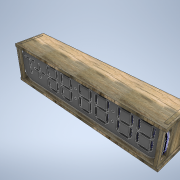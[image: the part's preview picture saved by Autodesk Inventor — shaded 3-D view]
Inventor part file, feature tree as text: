
AUTODESK INVENTOR PART (.ipt)
format: ipt  version: 2021 (Build 250183000, 183)  size: 3,486,208 bytes
history: native  units: in
note: dims shown in document units (in); Inventor stores cm internally (conversion verified against a paired STEP export)
features: other x71, extrude x17, sketch x16, imported_body x1
ambient origin geometry x8: Origin, YZ Plane, XZ Plane, XY Plane, X Axis, Y Axis, Z Axis, Center Point
bodies: Body1 (feature_tree), Body2 (feature_tree), Body3 (feature_tree), Body4 (feature_tree), Body5 (feature_tree), Body6 (feature_tree), Body7 (feature_tree)
feature tree (105):
  other  "Clock Face"
  other  "Blocks"
  extrude  "Extrusion1"  TaperAngle=135.0deg  [1 undecoded]
  extrude  "Extrusion3"  TaperAngle=135.0deg  [1 undecoded]
  extrude  "Extrusion5"  Depth=0.0433in
  extrude  "Extrusion6"  Depth=0.0433in
  extrude  "Extrusion9"  Depth=0.0433in
  extrude  "Extrusion7"  Depth=0.0433in
  extrude  "Extrusion10"  Depth=0.0433in
  extrude  "Extrusion8"  Depth=0.0433in
  extrude  "Extrusion13"  Depth=0.126in
  extrude  "Extrusion14"  Depth=0.126in
  extrude  "Extrusion15"  Depth=2.2441in
  extrude  "Extrusion16"  Depth=0.126in
  extrude  "Extrusion17"  Depth=0.126in
  extrude  "Extrusion18"  Depth=0.1969in
  extrude  "Extrusion19"  Depth=0.8661in
  extrude  "Extrusion20"  Depth=0.0866in
  extrude  "Extrusion21"  Depth=0.0118in
  other  "Single Segment"
  other  "7 Segment Digit"
  other  "Slanted Segment Large"
  other  "+ sign"
  other  "Dot"
  other  "Clock Face with T +-"
  other  "Clock Front Face Outline"
  other  "Small Segmemt"
  sketch  "Sketch5"  dims[d10=62.9921in d11=78.7402in d29=0.1969in d30=0.0in]
  sketch  "Sketch8"  dims[d105=0.0866in d108=0.0866in d111=0.0866in d112=0.0866in d113=0.0866in d114=0.0866in d115=0.0866in d116=0.0394in d117=0.1969in d121=0.0866in d122=0.0866in d126=135.0deg]
  other  "ClockBackface"
  sketch  "Sketch9"  dims[d127=0.8661in d128=135.0deg]
  sketch  "Sketch10"  dims[d129=0.0984in]
  other  "Backplace"
  sketch  "Sketch11"  dims[d131=0.0433in d132=0.0433in d137=0.0433in d138=0.0433in d139=0.0433in d140=0.0433in]
  other  "FrontCover"
  other  "7SegmentOutline"
  sketch  "Sketch15"  dims[d141=0.0433in d142=0.0433in]
  other  "Cable Trench"
  other  "Cable Trench Long"
  other  "CableCutouts"
  sketch  "Sketch17"  dims[d143=0.0433in d144=0.0433in]
  sketch  "Sketch20"  dims[d145=0.0433in d146=0.0433in]
  imported_body  "Base"
  sketch  "Sketch21"  dims[d150=0.0433in d151=0.0433in]
  other  "Side Panels"
  sketch  "Sketch22"  dims[d152=0.0433in d153=0.0433in]
  sketch  "Sketch23"  dims[d294=0.126in d295=0.126in]
  sketch  "Sketch25"  dims[d296=0.315in d297=0.126in]
  sketch  "Sketch26"  dims[d298=0.126in d299=2.2441in]
  other  "Top Panel"
  sketch  "Sketch27"  dims[d304=0.126in d305=0.126in]
  sketch  "Sketch28"  dims[d306=0.126in d307=0.126in]
  sketch  "Sketch29"  dims[d311=0.0787in d312=0.0787in d314=0.0787in d315=0.0787in d316=0.0787in d317=0.0787in d318=0.0787in d319=0.0787in d320=0.0394in d321=0.0394in d322=0.0394in d323=0.0394in d348=0.1969in d349=0.8661in d350=0.0866in d352=0.0118in d353=0.0118in d358=0.0118in d359=0.0118in d360=0.1969in d361=0.1969in d362=0.2953in d363=0.6693in d364=0.2953in d366=0.2953in d367=0.0in d368=0.0in d369=0.0in d370=0.0in d371=0.0in d372=0.5906in d373=0.0in d374=0.6299in d375=0.2362in d376=0.2362in d377=0.5354in d378=0.6299in d379=0.2362in d380=0.5906in d381=0.0in d402=1.9528in d429=12.9921in d430=2.7559in d431=0.9843in d462=0.0866in d463=0.0866in d464=0.0866in d465=0.0866in d466=0.0866in d467=0.0866in d468=0.0866in d469=0.0394in d470=0.1969in d471=0.0866in d472=0.0866in d473=135.0deg d474=0.6299in d475=135.0deg d476=0.0984in d477=0.1969in d478=0.6299in d479=0.0866in d480=0.0118in d481=0.0118in d482=0.0118in d483=0.0118in d496=0.0787in d497=0.0787in d501=0.0394in d502=0.0394in d503=0.0in d504=0.0in d505=0.039in d506=0.039in d507=0.039in d508=0.039in d509=0.8661in d510=0.9843in d511=0.9685in d514=0.0394in d515=0.0394in d516=0.0394in d517=0.0394in d518=0.0in d519=0.039in d520=0.4331in d522=0.9449in d523=0.0in d524=0.0591in d525=0.315in d526=0.2913in d527=0.8661in d528=0.6575in d529=0.315in d530=0.1969in d531=0.0in d536=1.378in d537=6.4961in d538=6.4961in d539=1.378in d542=1.378in d543=6.4961in d544=0.1181in d545=0.0in d549=0.1181in d550=0.0in d551=1.378in d552=6.4961in d553=0.1181in d554=0.0in d555=1.378in d556=6.4961in d557=0.1181in d558=0.0in d564=0.2362in d1135=1.1732in d1136=1.1732in d1137=2.1496in d1138=0.0612in d1139=0.0612in d1140=0.0612in d1143=0.0612in d1144=0.0612in d1145=90.0deg d1146=0.0866in d1147=0.0236in d1150=0.0236in d1153=0.0236in d1154=0.0866in d1155=1.0197in d1156=1.0197in d1157=0.0866in d1158=0.0236in d1159=0.0866in d1160=0.0866in d1161=0.0236in d1162=0.0866in d1163=0.0866in d1164=0.0236in d1165=0.0866in d1166=0.0866in d1167=0.0236in d1168=0.0866in d1169=0.0866in d1170=0.0866in d1171=0.0866in d1172=0.0866in d1173=0.0866in d1175=0.1102in d1176=0.8661in d1177=0.8661in d1178=1.0197in d1179=0.0866in d1180=0.0236in d1181=0.0866in d1182=0.0866in d1183=0.0236in d1184=0.0866in d1188=0.0866in d1189=0.0236in d1190=0.0866in d1193=0.0866in d1194=0.0236in d1195=0.0in d1196=0.0in d1198=135.0deg d1199=0.0612in d1200=0.0866in d1201=0.0in d1202=0.0in d1205=0.0in d1206=0.0in d1207=0.0in d1208=135.0deg d1209=90.0deg d1210=90.0deg d1211=0.0866in d1212=0.0236in d1213=0.6603in d1214=0.6603in d1215=0.6603in d1216=90.0deg d1217=135.0deg d1218=0.6603in d1219=0.0394in d1221=135.0deg d1222=0.0394in d1223=0.0866in d1224=0.0866in d1225=0.0866in d1227=0.0866in d1228=0.0866in d1229=0.0866in d1230=0.0236in d1231=135.0deg d1232=90.0deg d1233=90.0deg d1234=135.0deg d1235=90.0deg d1236=90.0deg d1239=0.1102in d1240=0.2402in d1241=0.2402in d1242=0.2835in d1243=0.2835in d1244=0.2402in d1245=0.2402in d1246=0.0669in d1247=0.0669in d1248=0.0669in d1249=0.0669in d1250=0.0433in d1251=0.0433in d1252=0.8661in d1253=0.1535in d1254=90.0deg d1255=135.0deg d1256=45.0deg d1257=0.6603in d1258=0.0236in d1259=135.0deg d1260=135.0deg d1261=90.0deg d1262=0.0612in d1263=0.0866in d1264=0.0in d1265=0.0in d1266=0.0in d1267=0.0in d1268=0.0in d1269=0.0in d1270=0.0in d1271=0.0in d1272=0.0in d1273=0.0in d1274=0.0in d1275=0.0in d1276=0.0in d1277=0.0in d1278=0.0in d1279=0.0in d1280=0.0in d1281=0.0in d1282=0.0in d1283=0.0in d1292=0.0866in d1307=0.0394in d1308=0.0394in d1309=0.0394in d1310=0.0394in d1311=0.0394in d1312=0.0394in d1313=0.0394in d1314=0.2756in d1315=0.0197in d1316=0.0197in d1317=0.3445in d1318=0.0394in d1319=0.0394in d1320=0.0787in d1321=0.0866in d1322=0.0787in d1323=0.0787in d1344=0.0394in d1350=0.0866in d1351=0.0866in d1386=0.1181in d1387=0.0in d1390=0.0394in d1392=0.0118in d1393=0.0394in d1394=0.0394in d1395=0.0394in d1396=0.0394in d1397=0.1378in d1398=0.1349in d1399=0.0394in d1402=0.0787in d1425=0.0in d1429=0.0in d1431=0.0394in d1432=0.0394in d1507=0.0in d1508=0.0394in d1509=0.0394in d1510=0.0394in d1511=0.0394in d1513=0.0394in d1514=0.0394in d1515=0.0in d1516=0.0in d1517=0.0in d1518=0.0in d1519=0.0197in d1520=0.0197in d1521=0.1969in d1522=0.0394in d1523=0.0394in d1524=0.0394in d1525=0.1181in d1526=0.1181in d1527=0.0394in d1529=0.2741in d1530=0.0787in d1531=0.0787in d1532=0.0325in d1533=0.033in d1534=0.0787in d1535=0.0787in d1536=0.0325in d1537=0.0787in d1538=0.0787in d1539=0.0325in d1635=0.0787in d1636=0.0689in d1638=0.2756in d1641=0.315in d1699=0.0197in d1700=0.0197in d1701=0.3445in d1702=0.0394in d1703=0.0394in d1704=0.0787in d1705=0.0787in d1706=0.0787in d1707=0.0in d1708=0.0394in d1709=0.0394in d1710=0.1462in d1711=0.0in d1712=0.0394in d1713=0.0394in d1714=0.0118in d1715=0.0394in d1716=0.0394in d1717=0.0394in d1718=0.0394in d1719=0.1378in d1720=0.1349in d1721=0.0394in d1722=0.0787in d1723=0.0787in d1724=0.0394in d1725=0.0394in d1726=0.0394in d1727=0.0394in d1728=0.0787in d1729=0.1181in d1730=0.0787in d1731=0.0394in d1732=0.0787in d1733=0.0787in d1734=0.0325in d1735=0.033in d1736=0.0787in d1737=0.0787in d1738=0.0325in d1739=0.0787in d1740=0.0787in d1741=0.0325in d1742=0.0325in d1747=0.2756in d1748=0.0984in d1749=0.0984in d1750=0.315in d1751=0.0325in d1752=0.0787in d1753=0.0787in d1754=0.0394in d1755=0.0394in d1756=0.0394in d1757=0.0394in d1758=0.0394in d1759=0.0394in d1760=0.0394in d1761=0.0394in d1762=0.0in d1763=0.0in d1764=0.0in d1765=0.0in d1766=0.0in d1767=0.0in d1768=0.0in d1769=0.0in d1770=0.1181in d1771=0.1181in d1772=0.4724in d1773=0.2362in d1774=0.0in d1775=0.0in d1776=0.0in d1777=0.0in d1778=0.0in d1779=0.0in d1780=0.0in d1781=0.0in d1782=0.2362in d1783=0.5906in d1784=0.1181in d1785=0.1181in d1786=0.0in d1787=0.0394in d1788=0.0394in d1789=0.0394in d1790=0.0394in d1791=0.0394in d1792=0.0394in d1793=0.0in d1794=0.0in d1795=0.0in d1796=0.0in d1797=0.0197in d1798=0.0197in d1799=0.1969in d1800=0.0394in d1801=0.0394in d1802=0.0394in d1803=0.1181in d1804=0.1181in d1805=0.0394in d1806=0.2741in d1808=0.0394in d1809=0.0394in d1810=0.0394in d1811=0.0394in d1812=0.0394in d1813=0.0394in d1814=0.0394in d1815=0.0394in d1840=0.0787in d1841=0.0787in d1842=0.501in d1843=0.0394in d1844=0.0394in d1845=90.0deg d1846=0.0in d1847=0.0in d1848=0.0in d1849=0.0in d1850=0.0in d1851=0.0in d1852=0.0in d1853=0.0in d1854=0.0in d1855=0.0in d1856=0.0in d1857=0.0in d1858=0.2756in d1859=0.0in d1860=0.0in d1861=0.0in d1862=0.2756in d1863=0.0in d1864=0.1181in d1865=0.0in d1898=0.0394in d1899=0.0591in d1900=0.0591in d1901=0.0591in d1902=0.0591in d1903=0.0591in d1904=0.0591in d1905=0.0394in d1906=0.2559in d1907=0.1772in d1908=0.1772in d1909=0.2559in d1910=0.1575in d1911=0.2362in d1912=0.2393in d1913=0.0197in d1914=0.3051in d1915=0.4066in d1916=0.3051in d1917=0.4066in d1918=0.0689in d1919=0.0689in d1920=0.0689in d1921=0.0in d1923=0.0335in d1924=0.0335in d1925=0.0335in d1926=0.0787in d1927=0.0335in d1940=0.2756in d1941=0.1181in d1942=0.1181in d1943=2.3622in d1944=0.2362in d1945=0.0in d1946=0.2362in d1948=0.0in d1949=0.0in d1950=0.2362in d1953=0.0in d1954=2.7559in d1955=0.0in d1956=0.1181in d1957=0.1181in d1958=0.2362in d1959=0.315in d1960=0.315in d1961=0.1181in d1962=0.2362in d1963=0.315in d1964=0.315in d1965=0.1181in d1966=0.2362in d1967=0.0in d1968=0.2362in d1969=0.315in d1970=0.315in d1971=0.0in d1972=0.0in d1973=0.2362in d1974=0.315in d1975=0.315in d1976=0.0in d1977=0.0in d1978=0.2362in d1979=0.0in d1980=0.0197in d1981=0.315in d1982=0.315in d1983=0.0in d1984=0.0in d1985=0.315in d1986=0.315in d1987=0.0in d1988=0.0in d1989=0.0197in d1990=0.2362in d1991=0.0in d1992=0.2362in d1993=0.0in d1994=0.2362in d1995=0.0in d1996=0.315in d1997=0.315in d1998=0.2362in d1999=0.0in d2000=0.315in d2001=0.315in d2002=0.2362in d2003=0.0in d2004=0.0in d2006=0.3386in d2007=0.3386in d2008=0.2362in d2009=0.0in d2010=0.0in d2011=0.3386in d2012=0.3386in d2013=0.0in d2014=0.0in d2015=0.2362in d2016=0.0in d2017=0.0in d2018=0.0in]
  other  "Single Segment:9"
  other  "Single Segment:10"
  other  "Single Segment:11"
  other  "Single Segment:12"
  other  "Single Segment:13"
  other  "Single Segment:14"
  other  "Single Segment:15"
  other  "7 Segment Digit:8"
  other  "7 Segment Digit:9"
  other  "7 Segment Digit:10"
  other  "7 Segment Digit:11"
  other  "7 Segment Digit:12"
  other  "7 Segment Digit:13"
  other  "Dot:7"
  other  "Dot:8"
  other  "Dot:9"
  other  "Dot:10"
  other  "Clock Front Face Outline:1"
  other  "Small Segmemt:1"
  other  "Small Segmemt:2"
  other  "Small Segmemt:3"
  other  "Small Segmemt:4"
  other  "+ sign:1"
  other  "Small Segmemt:5"
  other  "Small Segmemt:6"
  other  "Small Segmemt:7"
  other  "Small Segmemt:8"
  other  "Clock Face with T +-:1"
  other  "Clock Front Face Outline:2"
  other  "Clock Front Face Outline:3"
  other  "Clock Front Face Outline:4"
  other  "7SegmentOutline:1"
  other  "7SegmentOutline:2"
  other  "7SegmentOutline:3"
  other  "7SegmentOutline:4"
  other  "7SegmentOutline:5"
  other  "7SegmentOutline:6"
  other  "Dot:11"
  other  "Dot:12"
  other  "Dot:13"
  other  "Dot:14"
  other  "Cable Trench:3"
  other  "Cable Trench:4"
  other  "Cable Trench:5"
  other  "Cable Trench Long:4"
  other  "Cable Trench Long:5"
  other  "CableCutouts:3"
  other  "CableCutouts:4"
  other  "CableCutouts:5"
  other  "CableCutouts:6"
  other  "CableCutouts:7"
  other  "CableCutouts:8"
note: 2 required parameter values undecoded (feature->parameter linkage not recoverable at this tier; creation-order binding heuristic only, values carry confidence <= 0.55)
